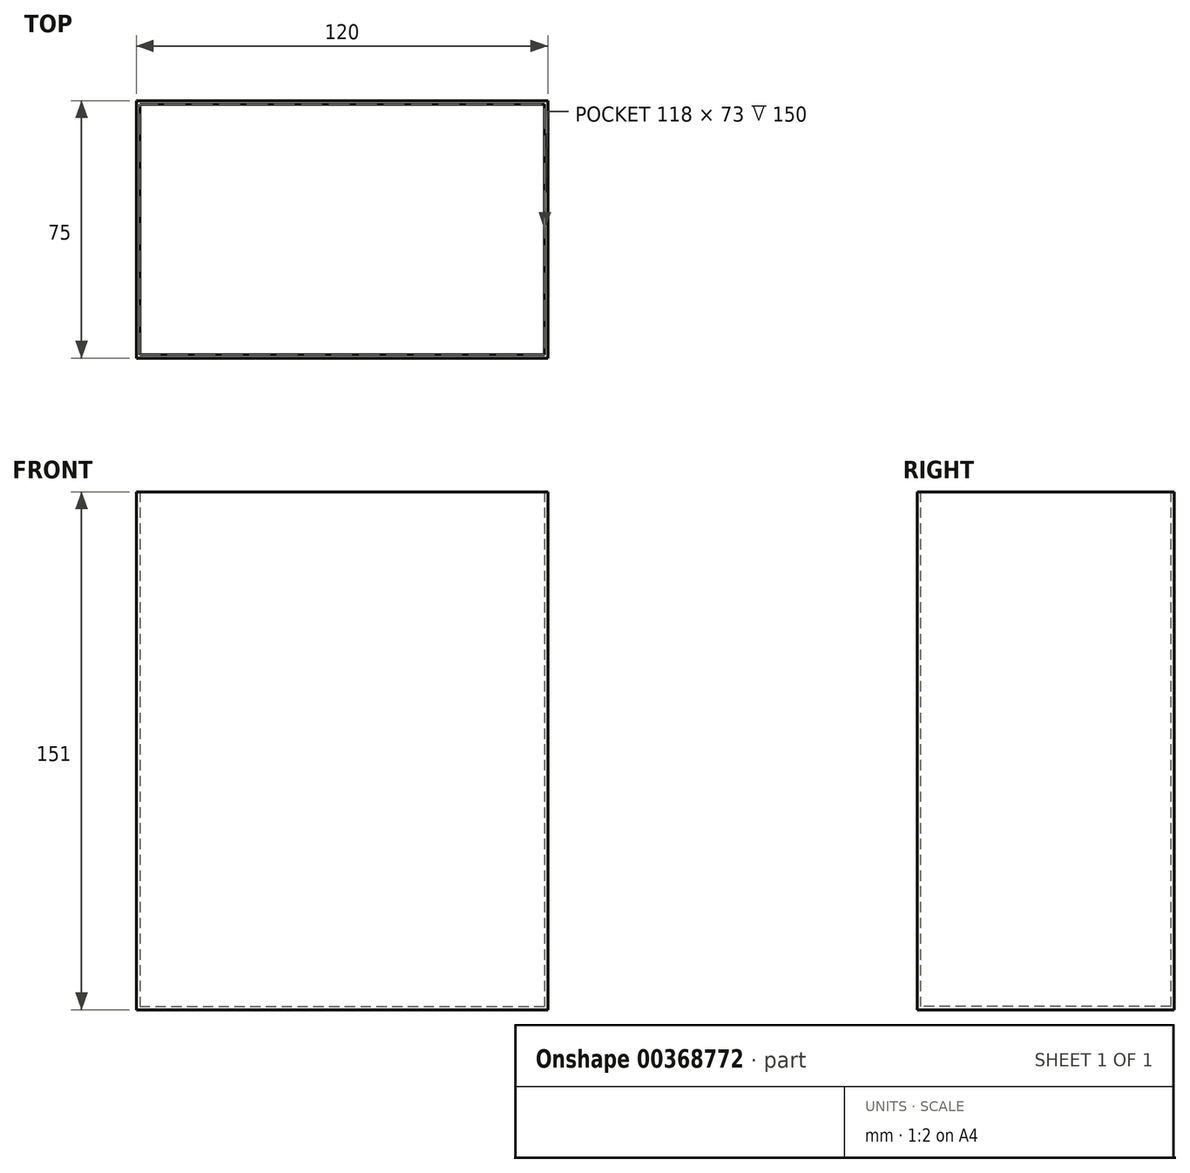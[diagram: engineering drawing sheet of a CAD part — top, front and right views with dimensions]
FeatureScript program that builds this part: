
annotation { "Feature Type Name" : "Feature", "Feature Type Description" : "" }
export const myFeature = defineFeature(function(context is Context, id is Id, definition is map)
    precondition{}
    {
        {
            var Q0;
            Q0=qCreatedBy(makeId("Top.planeOp"),FACE);
            var sketch = newSketch(context, id + "F0", { "sketchPlane" : qUnion([Q0])});
            skLineSegment(sketch, "E0.bottom", {"start": v(-42.81, 28.37) * mm, "end": v(77.19, 28.37) * mm});
            skLineSegment(sketch, "E0.top", {"start": v(-42.81, -46.63) * mm, "end": v(77.19, -46.63) * mm});
            skLineSegment(sketch, "E0.left", {"start": v(-42.81, 28.37) * mm, "end": v(-42.81, -46.63) * mm});
            skLineSegment(sketch, "E0.right", {"start": v(77.19, 28.37) * mm, "end": v(77.19, -46.63) * mm});
            skSolve(sketch);
        }
        {
            var Q0;
            Q0=qCreatedBy(makeId("Top.planeOp"),FACE);
            var sketch = newSketch(context, id + "F1", { "sketchPlane" : qUnion([Q0])});
            skLineSegment(sketch, "E1.bottom", {"start": v(-42.81, 28.37) * mm, "end": v(77.19, 28.37) * mm});
            skLineSegment(sketch, "E1.top", {"start": v(-42.81, -46.63) * mm, "end": v(77.19, -46.63) * mm});
            skLineSegment(sketch, "E1.left", {"start": v(-42.81, 28.37) * mm, "end": v(-42.81, -46.63) * mm});
            skLineSegment(sketch, "E1.right", {"start": v(77.19, 28.37) * mm, "end": v(77.19, -46.63) * mm});
            skLineSegment(sketch, "E2.0", {"start": v(76.19, 27.37) * mm, "end": v(76.19, -45.63) * mm});
            skLineSegment(sketch, "E2.1", {"start": v(-41.81, 27.37) * mm, "end": v(76.19, 27.37) * mm});
            skLineSegment(sketch, "E2.2", {"start": v(-41.81, 27.37) * mm, "end": v(-41.81, -45.63) * mm});
            skLineSegment(sketch, "E2.3", {"start": v(-41.81, -45.63) * mm, "end": v(76.19, -45.63) * mm});
            skSolve(sketch);
        }
        {
            var Q0;
            Q0 = qSketchRegion(id + "F0", true);
            extrude(context, id + "F2", {"entities" : qUnion([Q0]), "oppositeDirection" : true, "depth" : 1 * mm});
        }
        {
            var Q0;
            Q0 = qSketchRegion(id + "F1", true);
            extrude(context, id + "F3", {"entities" : qUnion([Q0]), "operationType" : NewBodyOperationType.ADD, "depth" : 150 * mm});
        }
    });
